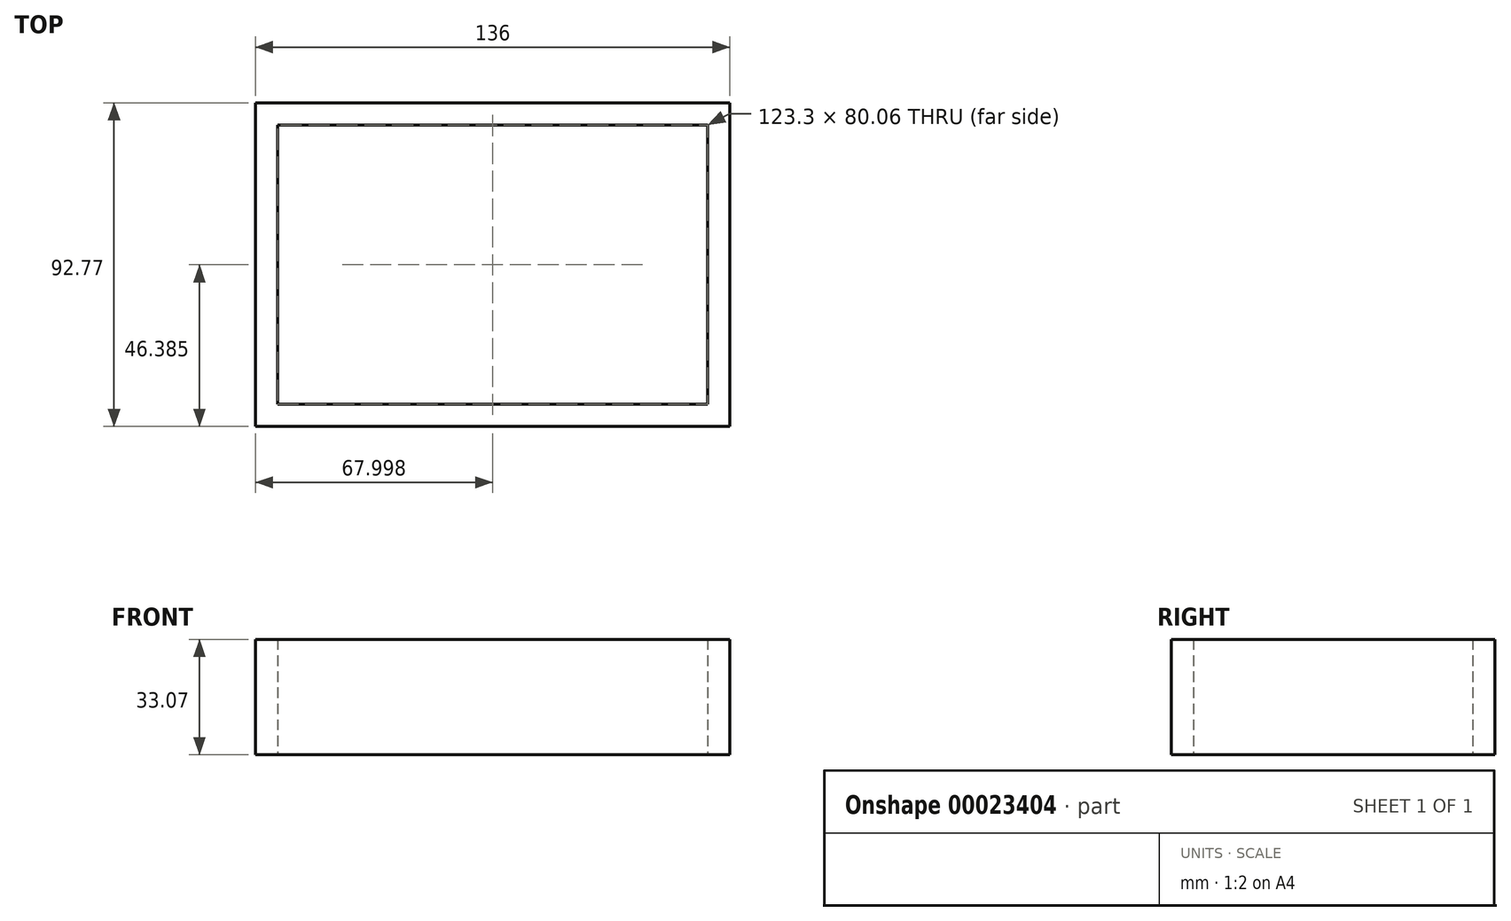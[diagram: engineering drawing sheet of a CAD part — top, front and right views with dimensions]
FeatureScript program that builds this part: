
annotation { "Feature Type Name" : "Feature", "Feature Type Description" : "" }
export const myFeature = defineFeature(function(context is Context, id is Id, definition is map)
    precondition{}
    {
        {
            var Q0;
            Q0=qCreatedBy(makeId("Top.planeOp"),FACE);
            var sketch = newSketch(context, id + "F0", { "sketchPlane" : qUnion([Q0])});
            skLineSegment(sketch, "E0.bottom", {"start": v(-68.01, 46.95) * mm, "end": v(67.99, 46.95) * mm});
            skLineSegment(sketch, "E0.top", {"start": v(-68.01, -45.82) * mm, "end": v(67.99, -45.82) * mm});
            skLineSegment(sketch, "E0.left", {"start": v(-68.01, 46.95) * mm, "end": v(-68.01, -45.82) * mm});
            skLineSegment(sketch, "E0.right", {"start": v(67.99, 46.95) * mm, "end": v(67.99, -45.82) * mm});
            skLineSegment(sketch, "E1.0", {"start": v(-61.66, 40.6) * mm, "end": v(61.64, 40.6) * mm});
            skLineSegment(sketch, "E1.1", {"start": v(-61.66, 40.6) * mm, "end": v(-61.66, -39.47) * mm});
            skLineSegment(sketch, "E1.2", {"start": v(-61.66, -39.47) * mm, "end": v(61.64, -39.47) * mm});
            skLineSegment(sketch, "E1.3", {"start": v(61.64, 40.6) * mm, "end": v(61.64, -39.47) * mm});
            skSolve(sketch);
        }
        {
            var Q0;
            Q0=makeQuery(id+"F0.imprint","IMPRINT",FACE,{"disambiguationData":[TD([[makeQuery(id+"F0.imprint","IMPRINT",EDGE,{"derivedFrom":sQuery(id+"F0.wireOp",EDGE,"E0.bottom")}),-1.0]])]});
            extrude(context, id + "F1", {"entities" : qUnion([Q0]), "depth" : 33.07 * mm});
        }
    });
